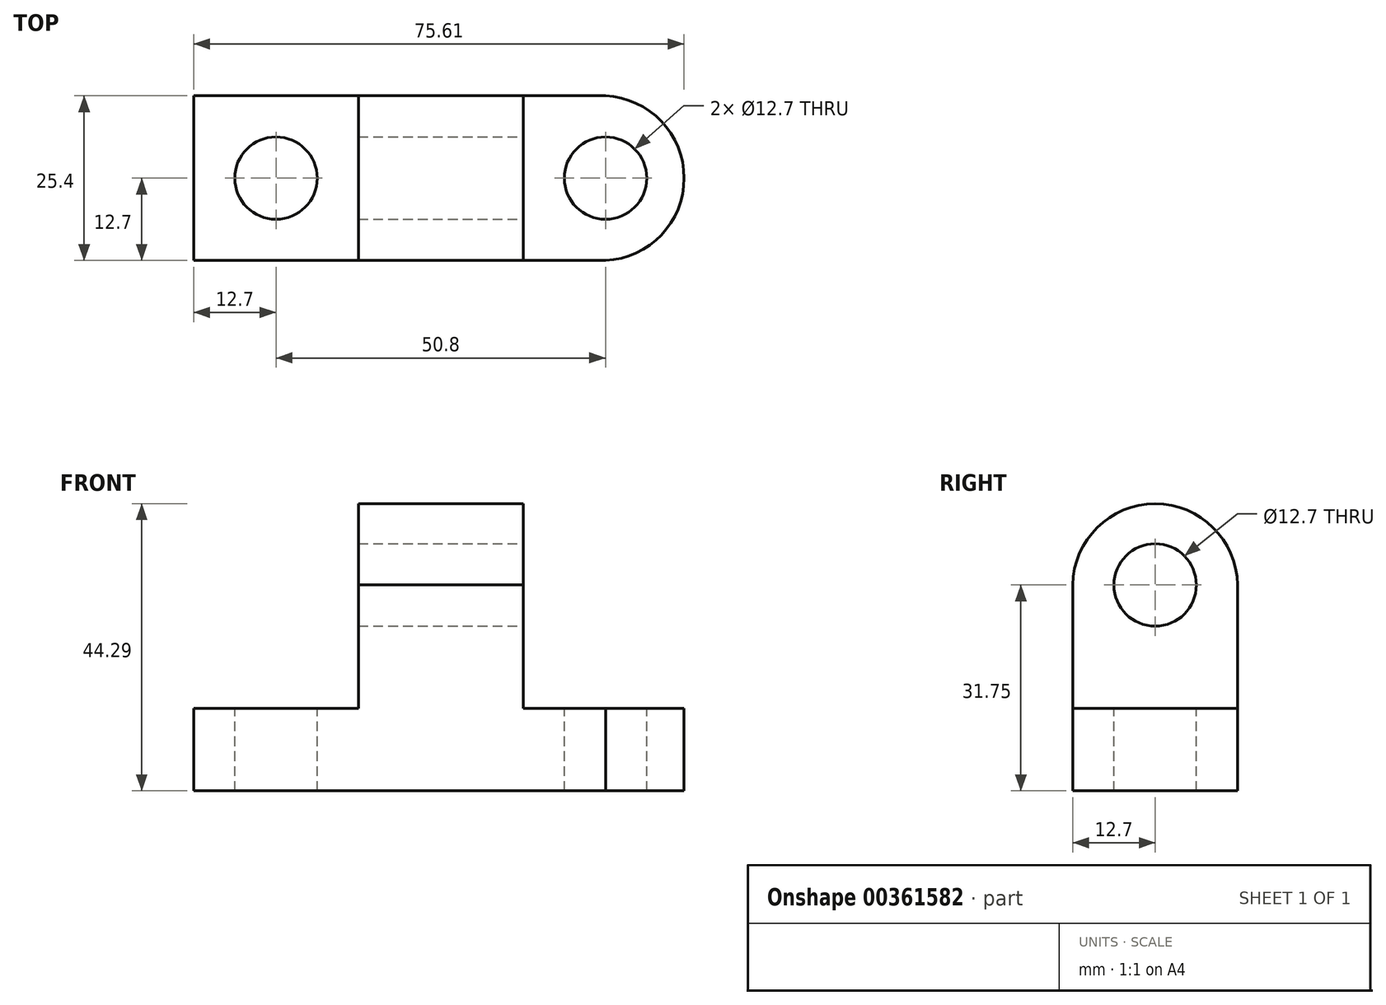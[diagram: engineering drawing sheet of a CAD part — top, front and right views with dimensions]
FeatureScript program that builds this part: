
annotation { "Feature Type Name" : "Feature", "Feature Type Description" : "" }
export const myFeature = defineFeature(function(context is Context, id is Id, definition is map)
    precondition{}
    {
        {
            var Q0;
            Q0=qCreatedBy(makeId("Front.planeOp"),FACE);
            var sketch = newSketch(context, id + "F0", { "sketchPlane" : qUnion([Q0])});
            skLineSegment(sketch, "E0", {"start": v(0, 0) * mm, "end": v(76.2, 0) * mm});
            skLineSegment(sketch, "E1", {"start": v(76.2, 0) * mm, "end": v(76.2, 44.45) * mm});
            skLineSegment(sketch, "E2", {"start": v(76.2, 44.45) * mm, "end": v(0, 44.45) * mm});
            skLineSegment(sketch, "E3", {"start": v(0, 44.45) * mm, "end": v(0, 0) * mm});
            skSolve(sketch);
        }
        {
            var Q0;
            Q0=makeQuery(id+"F0.imprint","IMPRINT",FACE,{"disambiguationData":[TD([[makeQuery(id+"F0.imprint","IMPRINT",EDGE,{"derivedFrom":sQuery(id+"F0.wireOp",EDGE,"E0")}),1.0]])]});
            extrude(context, id + "F1", {"entities" : qUnion([Q0]), "depth" : 25.4 * mm});
        }
        {
            var Q0;
            Q0=makeQuery(id+"F1.opExtrude","CAP_FACE",FACE,{"disambiguationData":[OSD([sQuery(id+"F0.wireOp",EDGE,"E0"),sQuery(id+"F0.wireOp",EDGE,"E1"),sQuery(id+"F0.wireOp",EDGE,"E2"),sQuery(id+"F0.wireOp",EDGE,"E3")])],"isStart":false});
            var sketch = newSketch(context, id + "F2", { "sketchPlane" : qUnion([Q0])});
            skLineSegment(sketch, "E4", {"start": v(0, 12.7) * mm, "end": v(25.4, 12.7) * mm});
            skLineSegment(sketch, "E5", {"start": v(25.4, 12.7) * mm, "end": v(25.4, 44.45) * mm});
            skLineSegment(sketch, "E6", {"start": v(25.4, 44.45) * mm, "end": v(0, 44.45) * mm});
            skLineSegment(sketch, "E7", {"start": v(0, 44.45) * mm, "end": v(0, 12.7) * mm});
            skLineSegment(sketch, "E8", {"start": v(25.4, 44.45) * mm, "end": v(50.8, 44.45) * mm});
            skLineSegment(sketch, "E9", {"start": v(50.8, 44.45) * mm, "end": v(50.8, 12.7) * mm});
            skLineSegment(sketch, "E10", {"start": v(50.8, 12.7) * mm, "end": v(76.2, 12.7) * mm});
            skLineSegment(sketch, "E11", {"start": v(76.2, 12.7) * mm, "end": v(76.2, 44.45) * mm});
            skLineSegment(sketch, "E12", {"start": v(76.2, 44.45) * mm, "end": v(50.8, 44.45) * mm});
            skSolve(sketch);
        }
        {
            var Q0;
            Q0=makeQuery(id+"F2.imprint","IMPRINT",FACE,{"disambiguationData":[TD([[makeQuery(id+"F2.imprint","IMPRINT",EDGE,{"derivedFrom":sQuery(id+"F2.wireOp",EDGE,"E4")}),1.0]])]});
            var Q1;
            Q1=makeQuery(id+"F2.imprint","IMPRINT",FACE,{"disambiguationData":[TD([[makeQuery(id+"F2.imprint","IMPRINT",EDGE,{"derivedFrom":sQuery(id+"F2.wireOp",EDGE,"E9")}),1.0]])]});
            extrude(context, id + "F3", {"entities" : qUnion([Q0, Q1]), "operationType" : NewBodyOperationType.REMOVE, "oppositeDirection" : true, "depth" : 25.4 * mm});
        }
        {
            var Q0;
            Q0=makeQuery(id+"F3.boolean.opBoolean","COPY",FACE,{"derivedFrom":makeQuery(id+"F3.opExtrude","SWEPT_FACE",FACE,{"disambiguationData":[OSD([sQuery(id+"F2.wireOp",EDGE,"E9")])]})});
            var sketch = newSketch(context, id + "F4", { "sketchPlane" : qUnion([Q0])});
            skCircle(sketch, "E13", {"center": v(-12.7, 31.75) * mm, "radius": 6.35 * mm});
            skArc(sketch, "E14", {"start": v(0, 31.75) * mm, "mid": v(-12.7, 44.29) * mm, "end": v(-25.4, 31.75) * mm});
            skSolve(sketch);
        }
        {
            var Q0;
            Q0=makeQuery(id+"F4.imprint","IMPRINT",FACE,{"disambiguationData":[TD([[makeQuery(id+"F4.imprint","IMPRINT",EDGE,{"derivedFrom":sQuery(id+"F4.wireOp",EDGE,"E13")}),1.0]])]});
            var Q1;
            {var subQ0=sQuery(id+"F4.wireOp",EDGE,"E14");Q1=makeQuery(id+"F4.imprint","IMPRINT",FACE,{"disambiguationData":[TD([[makeQuery(id+"F4.imprint","IMPRINT",EDGE,{"derivedFrom":subQ0}),-1.0]])]});}
            extrude(context, id + "F5", {"entities" : qUnion([Q0, Q1]), "operationType" : NewBodyOperationType.REMOVE, "oppositeDirection" : true, "depth" : 25.4 * mm});
        }
        {
            var Q0;
            Q0=makeQuery(id+"F3.boolean.opBoolean","COPY",FACE,{"derivedFrom":makeQuery(id+"F3.opExtrude","SWEPT_FACE",FACE,{"disambiguationData":[OSD([sQuery(id+"F2.wireOp",EDGE,"E4")])]})});
            var sketch = newSketch(context, id + "F6", { "sketchPlane" : qUnion([Q0])});
            skCircle(sketch, "E15", {"center": v(12.7, -12.7) * mm, "radius": 6.35 * mm});
            skArc(sketch, "E16", {"start": v(12.7, 0) * mm, "mid": v(-0.07, -12.7) * mm, "end": v(12.7, -25.4) * mm});
            skSolve(sketch);
        }
        {
            var Q0;
            Q0=makeQuery(id+"F6.imprint","IMPRINT",FACE,{"disambiguationData":[TD([[makeQuery(id+"F6.imprint","IMPRINT",EDGE,{"derivedFrom":sQuery(id+"F6.wireOp",EDGE,"E15")}),1.0]])]});
            var Q1;
            {var subQ0=sQuery(id+"F6.wireOp",EDGE,"E16");var subQ1=sQuery(id+"F2.wireOp",EDGE,"E4");var subQ2=makeQuery(id+"F3.boolean.opBoolean","COPY",EDGE,{"derivedFrom":makeQuery(id+"F3.opExtrude","CAP_EDGE",EDGE,{"disambiguationData":[OSD([subQ1])],"isStart":false})});var subQ3=makeQuery(id+"F6.imprint","INTERSECT",VERTEX,{"disambiguationData":[OD(1.0)],"derivedFrom":[subQ2,subQ0]});Q1=makeQuery(id+"F6.imprint","IMPRINT",FACE,{"disambiguationData":[TD([[makeQuery(id+"F6.imprint","IMPRINT",EDGE,{"disambiguationData":[TD([[subQ3,-1.0]])],"derivedFrom":subQ0}),-1.0]])]});}
            var Q2;
            {var subQ0=sQuery(id+"F6.wireOp",EDGE,"E16");var subQ1=sQuery(id+"F2.wireOp",EDGE,"E4");var subQ4=makeQuery(id+"F3.boolean.opBoolean","COPY",EDGE,{"derivedFrom":makeQuery(id+"F3.opExtrude","CAP_EDGE",EDGE,{"disambiguationData":[OSD([subQ1])],"isStart":true})});var subQ5=makeQuery(id+"F6.imprint","INTERSECT",VERTEX,{"disambiguationData":[OD(1.0)],"derivedFrom":[subQ4,subQ0]});Q2=makeQuery(id+"F6.imprint","IMPRINT",FACE,{"disambiguationData":[TD([[makeQuery(id+"F6.imprint","IMPRINT",EDGE,{"disambiguationData":[TD([[subQ5,1.0]])],"derivedFrom":subQ0}),-1.0]])]});}
            extrude(context, id + "F7", {"entities" : qUnion([Q0, Q1, Q2]), "operationType" : NewBodyOperationType.REMOVE, "oppositeDirection" : true, "depth" : 12.7 * mm});
        }
        {
            var Q0;
            Q0=makeQuery(id+"F3.boolean.opBoolean","COPY",FACE,{"derivedFrom":makeQuery(id+"F3.opExtrude","SWEPT_FACE",FACE,{"disambiguationData":[OSD([sQuery(id+"F2.wireOp",EDGE,"E10")])]})});
            var sketch = newSketch(context, id + "F8", { "sketchPlane" : qUnion([Q0])});
            skCircle(sketch, "E17", {"center": v(63.5, -12.7) * mm, "radius": 6.35 * mm});
            skArc(sketch, "E18", {"start": v(63.5, -25.4) * mm, "mid": v(75.61, -12.7) * mm, "end": v(63.5, 0) * mm});
            skSolve(sketch);
        }
        {
            var Q0;
            Q0=makeQuery(id+"F8.imprint","IMPRINT",FACE,{"disambiguationData":[TD([[makeQuery(id+"F8.imprint","IMPRINT",EDGE,{"derivedFrom":sQuery(id+"F8.wireOp",EDGE,"E17")}),1.0]])]});
            var Q1;
            {var subQ0=sQuery(id+"F8.wireOp",EDGE,"E18");Q1=makeQuery(id+"F8.imprint","IMPRINT",FACE,{"disambiguationData":[TD([[makeQuery(id+"F8.imprint","IMPRINT",EDGE,{"derivedFrom":subQ0}),-1.0]])]});}
            extrude(context, id + "F9", {"entities" : qUnion([Q0, Q1]), "operationType" : NewBodyOperationType.REMOVE, "oppositeDirection" : true, "depth" : 12.7 * mm});
        }
    });
